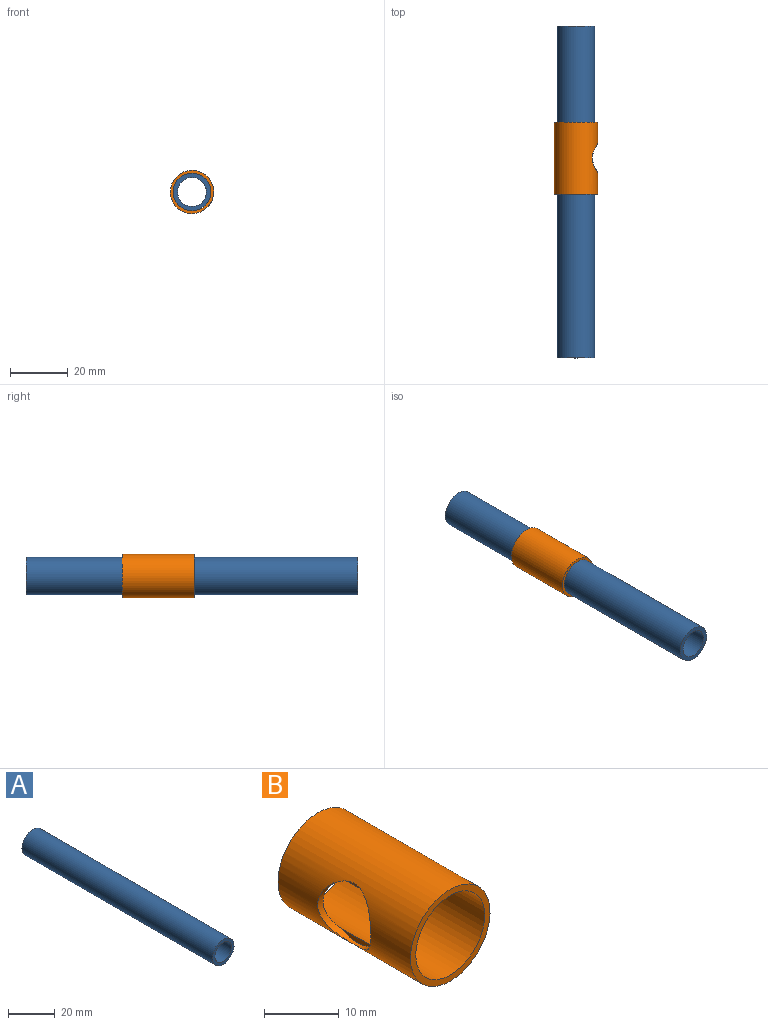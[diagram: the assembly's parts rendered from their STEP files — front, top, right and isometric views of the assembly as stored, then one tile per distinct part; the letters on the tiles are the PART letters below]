
ASSEMBLY  parts=2 mates=1
PART A: 7 faces, bbox 13x115x13 mm
  f0: cylinder r=6.5mm len=115mm, axis (0,1,0), area 4610.4mm2, adj f1,f2,f4
  f1: plane 13x13mm, normal (0,-1,0), area 54.2mm2, adj f0,f3
  f2: plane 13x13mm, normal (0,1,0), area 54.2mm2, adj f0,f3
  f3: cylinder r=5mm len=115mm, axis (0,1,0), area 3542.5mm2, adj f1,f2,f4,f5,f6
  f4: cylinder r=5mm len=10mm, axis (1,0,0), area 42.8mm2, adj f0,f3,f5,f6
  f5: plane 7.11x1.49mm, normal (1,0,0), area 7.3mm2, adj f3,f4
  f6: plane 7.11x1.49mm, normal (1,0,0), area 7.3mm2, adj f3,f4
PART B: 7 faces, bbox 15x25x15 mm
  f0: cylinder r=6.5mm len=25mm, axis (0,-1,0), area 943.7mm2, adj f2,f3,f4,f5,f6
  f1: cylinder r=7.5mm len=25mm, axis (0,-1,0), area 1094.2mm2, adj f2,f3,f6
  f2: plane 15x15mm, normal (0,1,0), area 44mm2, adj f0,f1
  f3: plane 15x15mm, normal (0,-1,0), area 44mm2, adj f0,f1
  f4: plane 5.58x0.85mm, normal (-1,0,0), area 3.2mm2, adj f0,f6
  f5: plane 5.58x0.85mm, normal (-1,0,0), area 3.2mm2, adj f0,f6
  f6: cylinder r=5mm len=10mm, axis (-1,0,0), area 30.9mm2, adj f0,f1,f4,f5
PLACE A t=(-32.82,24.7,-20.78)mm fixed
PLACE B rot(axis=(0,1,0),179.2deg) t=(-13.09,-33.58,-20.49)mm
MATE cylindrical B.f0 <-> A.f0  axis (0,-1,0) through (-32.82,-21.08,-20.78)mm
